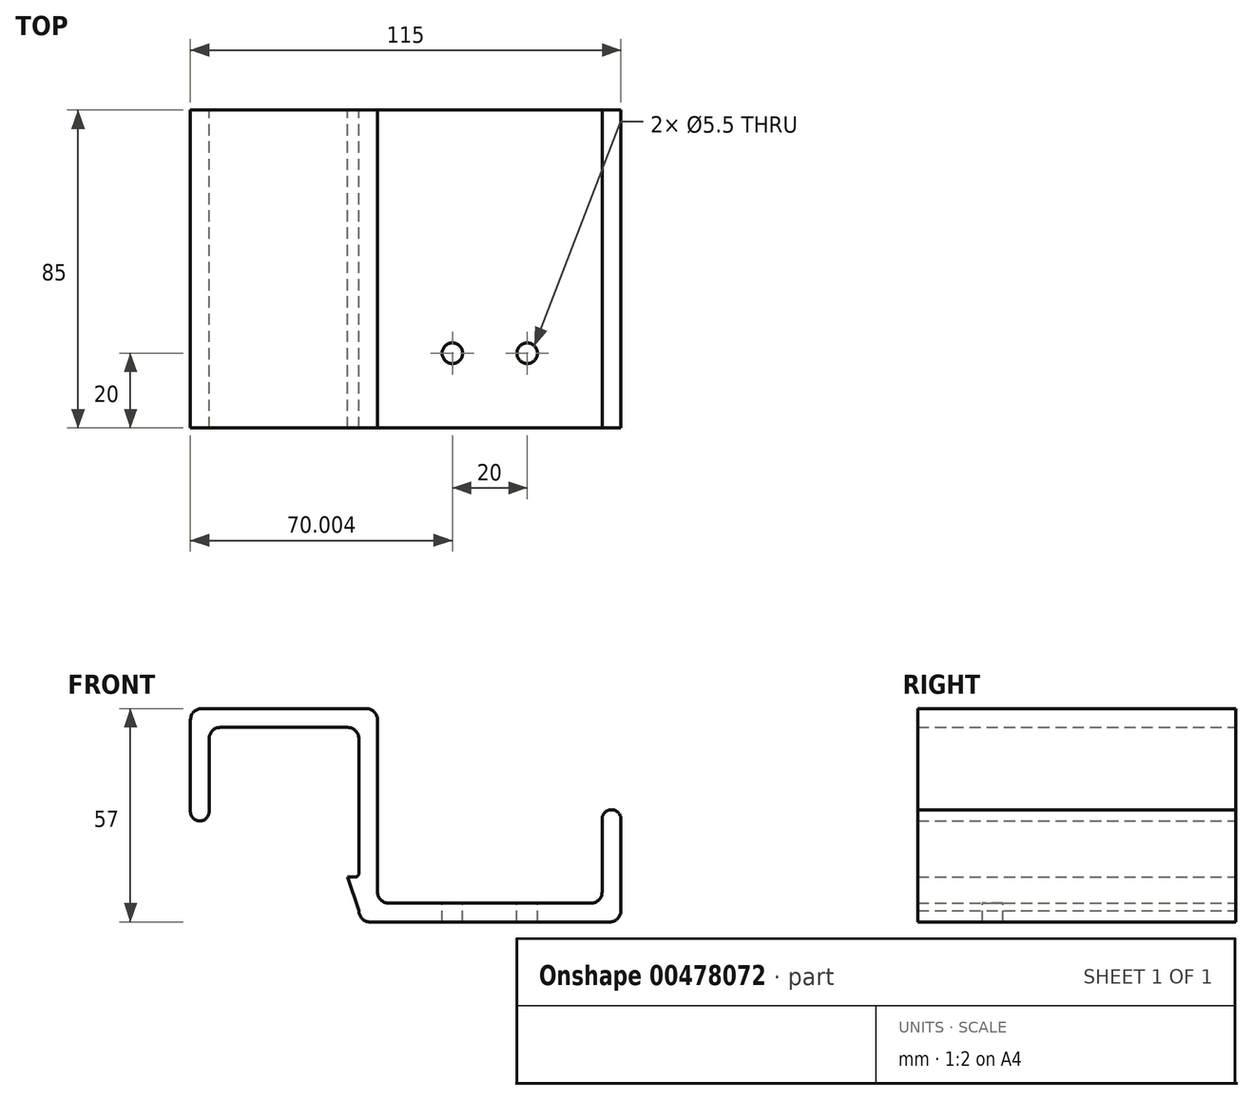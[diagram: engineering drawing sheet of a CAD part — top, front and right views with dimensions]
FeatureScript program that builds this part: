
annotation { "Feature Type Name" : "Feature", "Feature Type Description" : "" }
export const myFeature = defineFeature(function(context is Context, id is Id, definition is map)
    precondition{}
    {
        {
            var Q0;
            Q0=qCreatedBy(makeId("Front.planeOp"),FACE);
            var sketch = newSketch(context, id + "F0", { "sketchPlane" : qUnion([Q0])});
            skLineSegment(sketch, "E0", {"start": v(79, 28.85) * mm, "end": v(79, 28.85) * mm});
            skLineSegment(sketch, "E1", {"start": v(81.5, 26.35) * mm, "end": v(81.5, 1.85) * mm});
            skLineSegment(sketch, "E2", {"start": v(78.5, -1.15) * mm, "end": v(14.5, -1.15) * mm});
            skLineSegment(sketch, "E3", {"start": v(11.5, 11.85) * mm, "end": v(11.5, 47.85) * mm});
            skLineSegment(sketch, "E4", {"start": v(8.5, 50.85) * mm, "end": v(-25.5, 50.85) * mm});
            skLineSegment(sketch, "E5", {"start": v(-28.5, 47.85) * mm, "end": v(-28.5, 28.35) * mm});
            skLineSegment(sketch, "E6", {"start": v(-31, 25.85) * mm, "end": v(-31, 25.85) * mm});
            skLineSegment(sketch, "E7", {"start": v(-33.5, 28.35) * mm, "end": v(-33.5, 52.85) * mm});
            skLineSegment(sketch, "E8", {"start": v(-30.5, 55.85) * mm, "end": v(13.5, 55.85) * mm});
            skLineSegment(sketch, "E9", {"start": v(16.5, 52.85) * mm, "end": v(16.5, 6.85) * mm});
            skLineSegment(sketch, "E10", {"start": v(76.5, 26.35) * mm, "end": v(76.5, 6.85) * mm});
            skLineSegment(sketch, "E11", {"start": v(73.5, 3.85) * mm, "end": v(19.5, 3.85) * mm});
            skPoint(sketch, "E12.visualSharp", {"position": v(16.5, 55.85) * mm});
            skArc(sketch, "E12.filletArc", {"start": v(16.5, 52.85) * mm, "mid": v(15.63, 54.97) * mm, "end": v(13.5, 55.85) * mm});
            skPoint(sketch, "E13.visualSharp", {"position": v(11.5, 50.85) * mm});
            skArc(sketch, "E13.filletArc", {"start": v(11.5, 47.85) * mm, "mid": v(10.63, 49.97) * mm, "end": v(8.5, 50.85) * mm});
            skPoint(sketch, "E14.visualSharp", {"position": v(-28.5, 50.85) * mm});
            skArc(sketch, "E14.filletArc", {"start": v(-25.5, 50.85) * mm, "mid": v(-27.62, 49.97) * mm, "end": v(-28.5, 47.85) * mm});
            skPoint(sketch, "E15.visualSharp", {"position": v(-33.5, 55.85) * mm});
            skArc(sketch, "E15.filletArc", {"start": v(-30.5, 55.85) * mm, "mid": v(-32.62, 54.97) * mm, "end": v(-33.5, 52.85) * mm});
            skPoint(sketch, "E16.visualSharp", {"position": v(11.5, -1.15) * mm});
            skArc(sketch, "E16.filletArc", {"start": v(11.5, 1.85) * mm, "mid": v(12.38, -0.27) * mm, "end": v(14.5, -1.15) * mm});
            skPoint(sketch, "E17.visualSharp", {"position": v(76.5, 3.85) * mm});
            skArc(sketch, "E17.filletArc", {"start": v(73.5, 3.85) * mm, "mid": v(75.63, 4.73) * mm, "end": v(76.5, 6.85) * mm});
            skPoint(sketch, "E18.visualSharp", {"position": v(76.5, 28.85) * mm});
            skArc(sketch, "E18.filletArc", {"start": v(79, 28.85) * mm, "mid": v(77.24, 28.12) * mm, "end": v(76.5, 26.35) * mm});
            skPoint(sketch, "E19.visualSharp", {"position": v(81.5, 28.85) * mm});
            skArc(sketch, "E19.filletArc", {"start": v(81.5, 26.35) * mm, "mid": v(80.77, 28.12) * mm, "end": v(79, 28.85) * mm});
            skPoint(sketch, "E20.visualSharp", {"position": v(81.5, -1.15) * mm});
            skArc(sketch, "E20.filletArc", {"start": v(78.5, -1.15) * mm, "mid": v(80.63, -0.27) * mm, "end": v(81.5, 1.85) * mm});
            skArc(sketch, "E21", {"start": v(16.5, 6.85) * mm, "mid": v(17.38, 4.73) * mm, "end": v(19.5, 3.85) * mm});
            skPoint(sketch, "E22.orphan", {"position": v(16.5, 3.85) * mm});
            skPoint(sketch, "E23.visualSharp", {"position": v(-33.5, 25.85) * mm});
            skArc(sketch, "E23.filletArc", {"start": v(-33.5, 28.35) * mm, "mid": v(-32.76, 26.59) * mm, "end": v(-31, 25.85) * mm});
            skPoint(sketch, "E24.visualSharp", {"position": v(-28.5, 25.85) * mm});
            skArc(sketch, "E24.filletArc", {"start": v(-31, 25.85) * mm, "mid": v(-29.23, 26.59) * mm, "end": v(-28.5, 28.35) * mm});
            skLineSegment(sketch, "E25", {"start": v(10.5, 10.85) * mm, "end": v(8.5, 10.85) * mm});
            skLineSegment(sketch, "E26", {"start": v(8.5, 10.85) * mm, "end": v(11.5, 1.85) * mm});
            skPoint(sketch, "E27.visualSharp", {"position": v(11.5, 10.85) * mm});
            skArc(sketch, "E27.filletArc", {"start": v(10.5, 10.85) * mm, "mid": v(11.21, 11.15) * mm, "end": v(11.5, 11.85) * mm});
            skSolve(sketch);
        }
        {
            var Q0;
            Q0=makeQuery(id+"F0.imprint","IMPRINT",FACE,{"disambiguationData":[TD([[makeQuery(id+"F0.imprint","IMPRINT",EDGE,{"derivedFrom":sQuery(id+"F0.wireOp",EDGE,"E1")}),-1.0]])]});
            extrude(context, id + "F1", {"entities" : qUnion([Q0]), "endBound" : BoundingType.SYMMETRIC, "depth" : 85 * mm});
        }
        {
            var Q0;
            Q0=makeQuery(id+"F1.opExtrude","SWEPT_FACE",FACE,{"disambiguationData":[OSD([sQuery(id+"F0.wireOp",EDGE,"E11")])]});
            var sketch = newSketch(context, id + "F2", { "sketchPlane" : qUnion([Q0])});
            skLineSegment(sketch, "E28.0", {"start": v(73.5, -42.5) * mm, "end": v(19.5, -42.5) * mm, "construction": true});
            skLineSegment(sketch, "E29", {"start": v(73.5, -42.5) * mm, "end": v(56.5, -42.5) * mm, "construction": true});
            skLineSegment(sketch, "E30", {"start": v(56.5, -42.5) * mm, "end": v(56.5, -22.5) * mm, "construction": true});
            skLineSegment(sketch, "E31", {"start": v(56.5, -22.5) * mm, "end": v(36.5, -22.5) * mm, "construction": true});
            skCircle(sketch, "E32", {"center": v(36.5, -22.5) * mm, "radius": 2.75 * mm});
            skCircle(sketch, "E33", {"center": v(56.5, -22.5) * mm, "radius": 2.75 * mm});
            skSolve(sketch);
        }
        {
            var Q0;
            Q0=makeQuery(id+"F2.imprint","IMPRINT",FACE,{"disambiguationData":[TD([[makeQuery(id+"F2.imprint","IMPRINT",EDGE,{"derivedFrom":sQuery(id+"F2.wireOp",EDGE,"E32")}),1.0]])]});
            var Q1;
            Q1=makeQuery(id+"F2.imprint","IMPRINT",FACE,{"disambiguationData":[TD([[makeQuery(id+"F2.imprint","IMPRINT",EDGE,{"derivedFrom":sQuery(id+"F2.wireOp",EDGE,"E33")}),1.0]])]});
            extrude(context, id + "F3", {"entities" : qUnion([Q0, Q1]), "operationType" : NewBodyOperationType.REMOVE, "endBound" : BoundingType.THROUGH_ALL, "oppositeDirection" : true, "depth" : 25 * mm});
        }
    });
